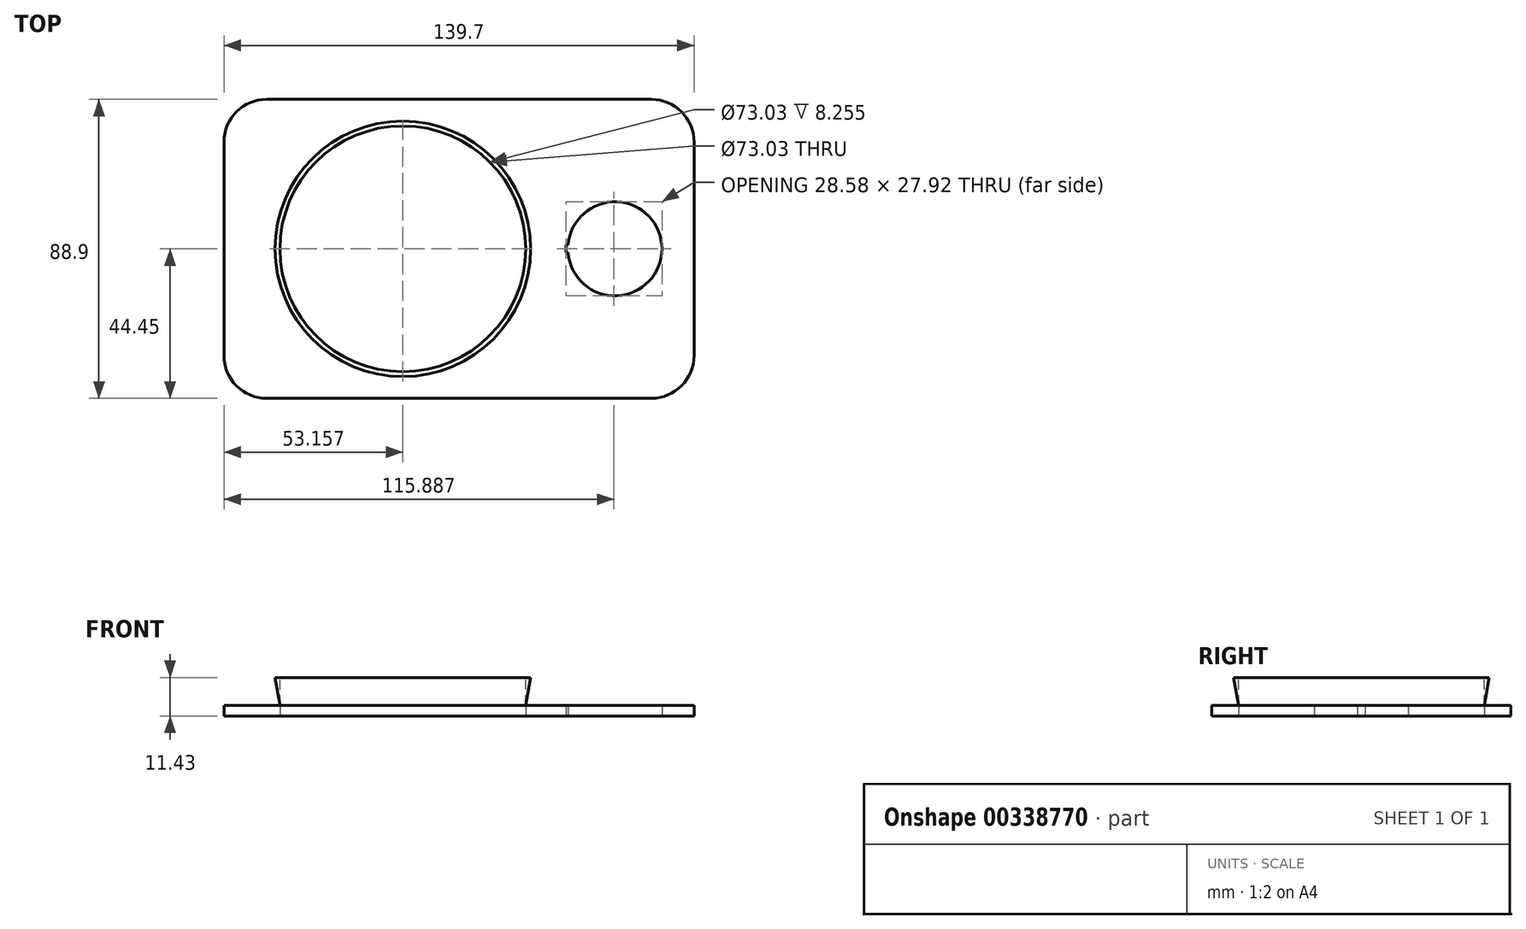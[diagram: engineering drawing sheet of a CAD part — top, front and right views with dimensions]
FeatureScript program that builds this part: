
annotation { "Feature Type Name" : "Feature", "Feature Type Description" : "" }
export const myFeature = defineFeature(function(context is Context, id is Id, definition is map)
    precondition{}
    {
        {
            var Q0;
            Q0=qCreatedBy(makeId("Top.planeOp"),FACE);
            var sketch = newSketch(context, id + "F0", { "sketchPlane" : qUnion([Q0])});
            skLineSegment(sketch, "E0.bottom", {"start": v(57.15, 44.45) * mm, "end": v(-57.15, 44.45) * mm});
            skLineSegment(sketch, "E0.top", {"start": v(57.15, -44.45) * mm, "end": v(-57.15, -44.45) * mm});
            skLineSegment(sketch, "E0.left", {"start": v(69.85, 31.75) * mm, "end": v(69.85, -31.75) * mm});
            skLineSegment(sketch, "E0.right", {"start": v(-69.85, 31.75) * mm, "end": v(-69.85, -31.75) * mm});
            skPoint(sketch, "E0.middle", {"position": v(0, 0) * mm});
            skPoint(sketch, "E1.visualSharp", {"position": v(-69.85, 44.45) * mm});
            skArc(sketch, "E1.filletArc", {"start": v(-57.15, 44.45) * mm, "mid": v(-66.13, 40.73) * mm, "end": v(-69.85, 31.75) * mm});
            skPoint(sketch, "E2.visualSharp", {"position": v(69.85, 44.45) * mm});
            skArc(sketch, "E2.filletArc", {"start": v(69.85, 31.75) * mm, "mid": v(66.13, 40.73) * mm, "end": v(57.15, 44.45) * mm});
            skPoint(sketch, "E3.visualSharp", {"position": v(69.85, -44.45) * mm});
            skArc(sketch, "E3.filletArc", {"start": v(57.15, -44.45) * mm, "mid": v(66.13, -40.73) * mm, "end": v(69.85, -31.75) * mm});
            skPoint(sketch, "E4.visualSharp", {"position": v(-69.85, -44.45) * mm});
            skArc(sketch, "E4.filletArc", {"start": v(-69.85, -31.75) * mm, "mid": v(-66.13, -40.73) * mm, "end": v(-57.15, -44.45) * mm});
            skCircle(sketch, "E5", {"center": v(-16.7, 0) * mm, "radius": 36.51 * mm});
            skLineSegment(sketch, "E6", {"start": v(69.85, 0) * mm, "end": v(46.36, 0) * mm});
            skPoint(sketch, "E6.endSnap0", {"position": v(69.85, 0) * mm});
            skArc(sketch, "E7", {"start": v(32.43, -1.14) * mm, "mid": v(60.33, 0) * mm, "end": v(32.43, 1.14) * mm});
            skLineSegment(sketch, "E8.bottom", {"start": v(31.75, -1.14) * mm, "end": v(32.43, -1.14) * mm});
            skLineSegment(sketch, "E8.top", {"start": v(31.75, 1.14) * mm, "end": v(32.43, 1.14) * mm});
            skLineSegment(sketch, "E8.left", {"start": v(31.75, -1.14) * mm, "end": v(31.75, 1.14) * mm});
            skPoint(sketch, "E8.middle", {"position": v(32.39, 0) * mm});
            skPoint(sketch, "E8.right.end.orphan", {"position": v(33.02, 1.14) * mm});
            skPoint(sketch, "E9.orphan", {"position": v(33.02, -1.14) * mm});
            skSolve(sketch);
        }
        {
            var Q0;
            Q0=makeQuery(id+"F0.imprint","IMPRINT",FACE,{"disambiguationData":[TD([[makeQuery(id+"F0.imprint","IMPRINT",EDGE,{"derivedFrom":sQuery(id+"F0.wireOp",EDGE,"E0.bottom")}),1.0]])]});
            extrude(context, id + "F1", {"entities" : qUnion([Q0]), "depth" : 3.17 * mm});
        }
        {
            var Q0;
            Q0=makeQuery(id+"F1.opExtrude","CAP_FACE",FACE,{"disambiguationData":[OSD([sQuery(id+"F0.wireOp",EDGE,"E0.bottom"),sQuery(id+"F0.wireOp",EDGE,"E0.top"),sQuery(id+"F0.wireOp",EDGE,"E0.left"),sQuery(id+"F0.wireOp",EDGE,"E0.right"),sQuery(id+"F0.wireOp",EDGE,"E1.filletArc"),sQuery(id+"F0.wireOp",EDGE,"E2.filletArc"),sQuery(id+"F0.wireOp",EDGE,"E3.filletArc"),sQuery(id+"F0.wireOp",EDGE,"E4.filletArc"),sQuery(id+"F0.wireOp",EDGE,"E5"),sQuery(id+"F0.wireOp",EDGE,"E7"),sQuery(id+"F0.wireOp",EDGE,"E8.bottom"),sQuery(id+"F0.wireOp",EDGE,"E8.top"),sQuery(id+"F0.wireOp",EDGE,"E8.left")])],"isStart":false});
            var sketch = newSketch(context, id + "F2", { "sketchPlane" : qUnion([Q0])});
            skCircle(sketch, "E10", {"center": v(-16.7, 0) * mm, "radius": 41.27 * mm});
            skSolve(sketch);
        }
        {
            var Q0;
            Q0=makeQuery(id+"F2.imprint","IMPRINT",FACE,{"disambiguationData":[TD([[makeQuery(id+"F2.imprint","IMPRINT",EDGE,{"derivedFrom":makeQuery(id+"F1.opExtrude","CAP_EDGE",EDGE,{"disambiguationData":[OSD([sQuery(id+"F0.wireOp",EDGE,"E5")])],"isStart":false})}),1.0]])]});
            extrude(context, id + "F3", {"entities" : qUnion([Q0]), "depth" : 8.25 * mm, "hasDraft" : true, "draftAngle" : 10 * degree});
        }
        {
            var Q0;
            Q0=makeQuery(id+"F3.opExtrude","CAP_FACE",FACE,{"disambiguationData":[OSD([sQuery(id+"F0.wireOp",EDGE,"E5")])],"isStart":false});
            var sketch = newSketch(context, id + "F4", { "sketchPlane" : qUnion([Q0])});
            skCircle(sketch, "E11", {"center": v(-16.7, 0) * mm, "radius": 36.51 * mm});
            skSolve(sketch);
        }
        {
            var Q0;
            Q0=makeQuery(id+"F4.imprint","IMPRINT",FACE,{"disambiguationData":[TD([[makeQuery(id+"F4.imprint","IMPRINT",EDGE,{"derivedFrom":sQuery(id+"F4.wireOp",EDGE,"E11")}),1.0]])]});
            extrude(context, id + "F5", {"entities" : qUnion([Q0]), "operationType" : NewBodyOperationType.REMOVE, "oppositeDirection" : true, "depth" : 8.25 * mm});
        }
    });
